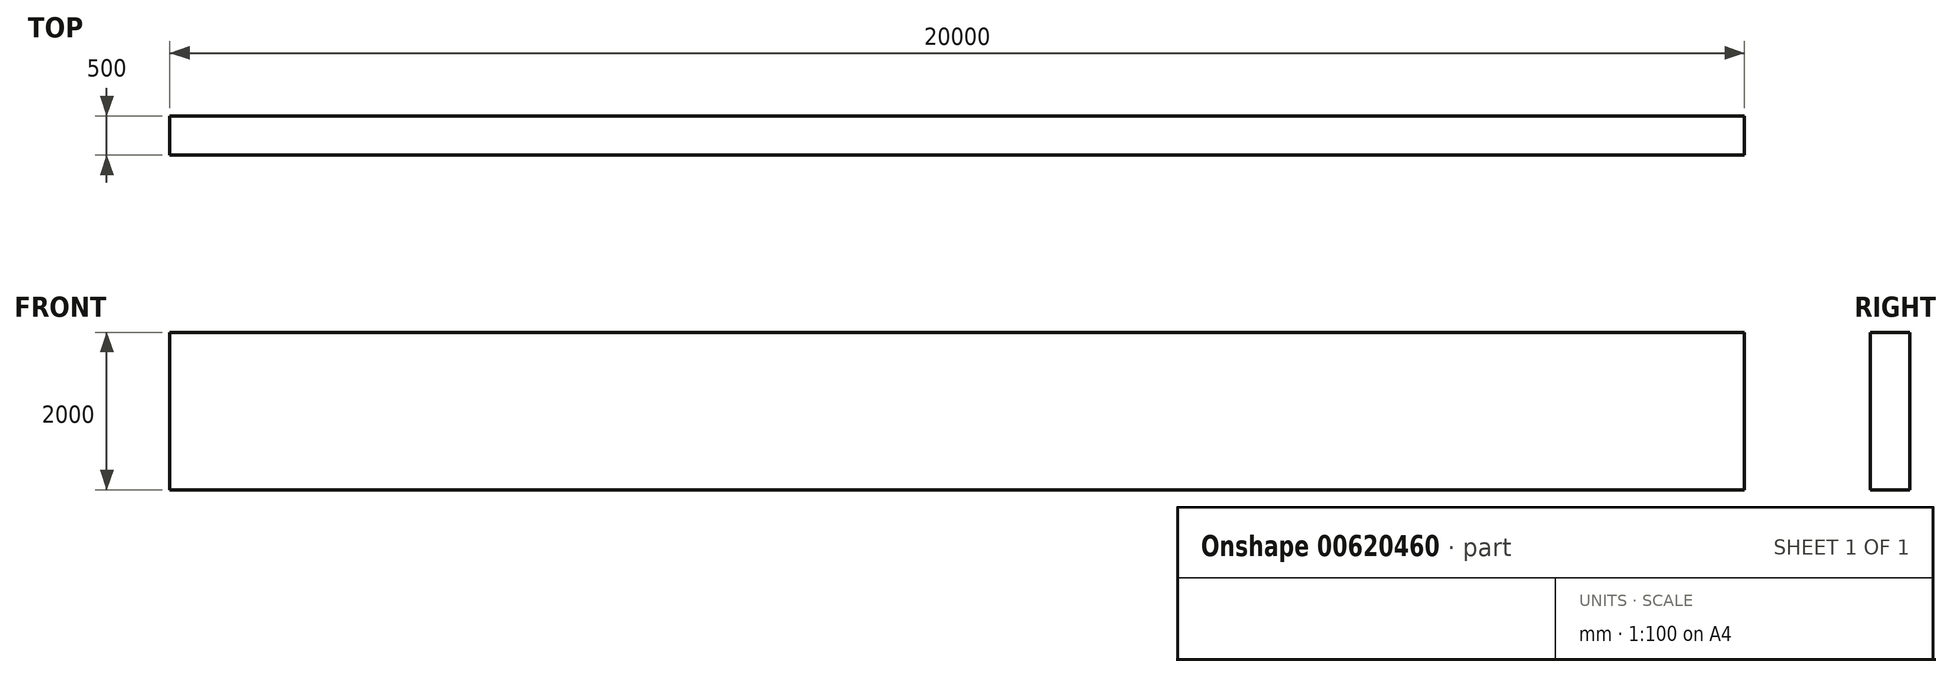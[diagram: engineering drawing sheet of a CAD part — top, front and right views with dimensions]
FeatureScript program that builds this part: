
annotation { "Feature Type Name" : "Feature", "Feature Type Description" : "" }
export const myFeature = defineFeature(function(context is Context, id is Id, definition is map)
    precondition{}
    {
        {
            var Q0;
            Q0=qCreatedBy(makeId("Front.planeOp"),FACE);
            var sketch = newSketch(context, id + "F0", { "sketchPlane" : qUnion([Q0])});
            skLineSegment(sketch, "E0.bottom", {"start": v(10000, -1000) * mm, "end": v(-10000, -1000) * mm});
            skLineSegment(sketch, "E0.top", {"start": v(10000, 1000) * mm, "end": v(-10000, 1000) * mm});
            skLineSegment(sketch, "E0.left", {"start": v(10000, -1000) * mm, "end": v(10000, 1000) * mm});
            skLineSegment(sketch, "E0.right", {"start": v(-10000, -1000) * mm, "end": v(-10000, 1000) * mm});
            skPoint(sketch, "E0.middle", {"position": v(0, 0) * mm});
            skSolve(sketch);
        }
        {
            var Q0;
            Q0=makeQuery(id+"F0.imprint","IMPRINT",FACE,{"disambiguationData":[TD([[makeQuery(id+"F0.imprint","IMPRINT",EDGE,{"derivedFrom":sQuery(id+"F0.wireOp",EDGE,"E0.bottom")}),-1.0]])]});
            extrude(context, id + "F1", {"entities" : qUnion([Q0]), "depth" : 500 * mm, "offsetDistance" : 25.4 * mm, "symmetric" : true});
        }
    });
